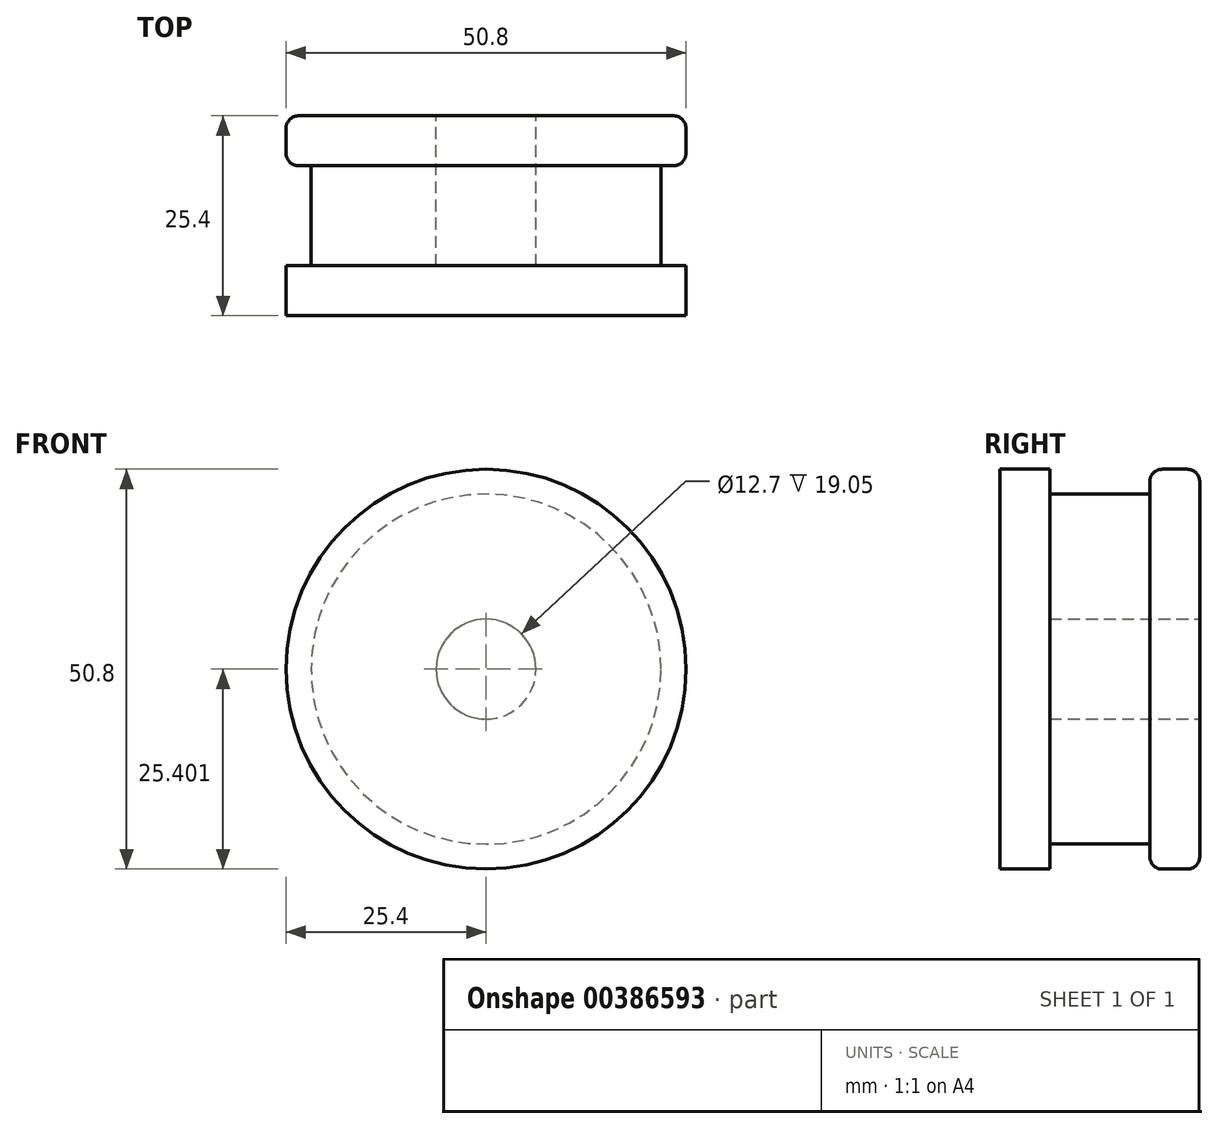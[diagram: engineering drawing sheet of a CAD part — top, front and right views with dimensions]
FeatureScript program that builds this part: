
annotation { "Feature Type Name" : "Feature", "Feature Type Description" : "" }
export const myFeature = defineFeature(function(context is Context, id is Id, definition is map)
    precondition{}
    {
        {
            var Q0;
            Q0=qCreatedBy(makeId("Front.planeOp"),FACE);
            var sketch = newSketch(context, id + "F0", { "sketchPlane" : qUnion([Q0])});
            skCircle(sketch, "E0", {"center": v(0, -3.23) * mm, "radius": 25.4 * mm});
            skSolve(sketch);
        }
        {
            var Q0;
            Q0 = qSketchRegion(id + "F0", true);
            extrude(context, id + "F1", {"entities" : qUnion([Q0]), "depth" : 6.35 * mm});
        }
        {
            var Q0;
            Q0=makeQuery(id+"F1.opExtrude","CAP_FACE",FACE,{"disambiguationData":[OSD([sQuery(id+"F0.wireOp",EDGE,"E0")])],"isStart":false});
            var sketch = newSketch(context, id + "F2", { "sketchPlane" : qUnion([Q0])});
            skCircle(sketch, "E1", {"center": v(0, -3.23) * mm, "radius": 22.23 * mm});
            skSolve(sketch);
        }
        {
            var Q0;
            Q0 = qSketchRegion(id + "F2", true);
            extrude(context, id + "F3", {"entities" : qUnion([Q0]), "operationType" : NewBodyOperationType.ADD, "depth" : 12.7 * mm});
        }
        {
            var Q0;
            Q0=makeQuery(id+"F3.opExtrude","CAP_FACE",FACE,{"disambiguationData":[OSD([sQuery(id+"F2.wireOp",EDGE,"E1")])],"isStart":false});
            var sketch = newSketch(context, id + "F4", { "sketchPlane" : qUnion([Q0])});
            skCircle(sketch, "E2", {"center": v(0, -3.23) * mm, "radius": 25.4 * mm});
            skSolve(sketch);
        }
        {
            var Q0;
            Q0=makeQuery(id+"F4.imprint","IMPRINT",FACE,{"disambiguationData":[TD([[makeQuery(id+"F4.imprint","IMPRINT",EDGE,{"derivedFrom":sQuery(id+"F4.wireOp",EDGE,"E2")}),1.0]])]});
            var Q1;
            Q1=makeQuery(id+"F4.imprint","IMPRINT",FACE,{"disambiguationData":[TD([[makeQuery(id+"F4.imprint","IMPRINT",EDGE,{"derivedFrom":makeQuery(id+"F3.opExtrude","CAP_EDGE",EDGE,{"disambiguationData":[OSD([sQuery(id+"F2.wireOp",EDGE,"E1")])],"isStart":false})}),1.0]])]});
            extrude(context, id + "F5", {"entities" : qUnion([Q0, Q1]), "operationType" : NewBodyOperationType.ADD, "depth" : 6.35 * mm});
        }
        {
            var Q0;
            Q0=makeQuery(id+"F5.opExtrude","CAP_FACE",FACE,{"disambiguationData":[OSD([sQuery(id+"F4.wireOp",EDGE,"E2")])],"isStart":false});
            var sketch = newSketch(context, id + "F6", { "sketchPlane" : qUnion([Q0])});
            skPoint(sketch, "E3", {"position": v(0, -3.23) * mm});
            skPoint(sketch, "E4", {"position": v(19.05, -3.23) * mm});
            skPoint(sketch, "E5", {"position": v(0, -22.28) * mm});
            skPoint(sketch, "E6", {"position": v(-19.05, -3.23) * mm});
            skPoint(sketch, "E7", {"position": v(0, 15.82) * mm});
            skSolve(sketch);
        }
        {
            var Q0;
            Q0=sQuery(id+"F6.wireOp",VERTEX,"E4");
            var Q1;
            Q1=sQuery(id+"F6.wireOp",VERTEX,"E5");
            var Q2;
            Q2=sQuery(id+"F6.wireOp",VERTEX,"E6");
            var Q3;
            Q3=sQuery(id+"F6.wireOp",VERTEX,"E7");
            var Q4;
            Q4=makeQuery(id+"F1.opExtrude","SWEPT_BODY",BODY,{"disambiguationData":[OSD([sQuery(id+"F0.wireOp",EDGE,"E0")])]});
            hole(context, id + "F7", {"style" : HoleStyle.SIMPLE, "endStyle" : HoleEndStyle.BLIND, "holeDiameter" : 3.17 * mm, "holeDepth" : 3.17 * mm, "isTappedThrough" : true, "tappedDepth" : 12.7 * mm, "tapClearance" : 3, "locations" : qUnion([Q0, Q1, Q2, Q3]), "scope" : qUnion([Q4])});
        }
        {
            var Q0;
            Q0=sQuery(id+"F0.wireOp",VERTEX,"E0.center");
            var Q1;
            Q1=makeQuery(id+"F1.opExtrude","SWEPT_BODY",BODY,{"disambiguationData":[OSD([sQuery(id+"F0.wireOp",EDGE,"E0")])]});
            hole(context, id + "F8", {"style" : HoleStyle.SIMPLE, "endStyle" : HoleEndStyle.THROUGH, "oppositeDirection" : true, "holeDiameter" : 12.7 * mm, "isTappedThrough" : true, "tappedDepth" : 12.7 * mm, "tapClearance" : 3, "locations" : qUnion([Q0]), "scope" : qUnion([Q1])});
        }
        {
            var Q0;
            Q0=makeQuery(id+"F1.opExtrude","CAP_EDGE",EDGE,{"disambiguationData":[OSD([sQuery(id+"F0.wireOp",EDGE,"E0")])],"isStart":false});
            var Q1;
            Q1=makeQuery(id+"F1.opExtrude","CAP_EDGE",EDGE,{"disambiguationData":[OSD([sQuery(id+"F0.wireOp",EDGE,"E0")])],"isStart":true});
            var Q2;
            Q2=makeQuery(id+"F3.opExtrude","CAP_EDGE",EDGE,{"disambiguationData":[OSD([sQuery(id+"F2.wireOp",EDGE,"E1")])],"isStart":true});
            var Q3;
            Q3=makeQuery(id+"F5.opExtrude","CAP_EDGE",EDGE,{"disambiguationData":[OSD([sQuery(id+"F4.wireOp",EDGE,"E2")])],"isStart":false});
            var Q4;
            Q4=makeQuery(id+"F5.opExtrude","CAP_EDGE",EDGE,{"disambiguationData":[OSD([sQuery(id+"F4.wireOp",EDGE,"E2")])],"isStart":true});
            var Q5;
            Q5=makeQuery(id+"F3.opExtrude","CAP_EDGE",EDGE,{"disambiguationData":[OSD([sQuery(id+"F2.wireOp",EDGE,"E1")])],"isStart":false});
            fillet(context, id + "F9", {"entities" : qUnion([Q0, Q1, Q2, Q3, Q4, Q5]), "radius" : 1.59 * mm, "tangentPropagation" : true, "allowEdgeOverflow" : false});
        }
        {
            var Q0;
            Q0 = qSketchRegion(id + "F4", true);
            extrude(context, id + "F10", {"entities" : qUnion([Q0]), "operationType" : NewBodyOperationType.ADD, "depth" : 6.35 * mm});
        }
    });
